# Revit family: Тумба медицинская общего назначения с выдвижным ящиком
name_source: partatom
category: Оборудование
revit_build: Autodesk Revit 2017 (Build: 20170419_0315(x64)
units: mm (PartAtom-declared; Revit-internal decimal feet)

## family parameters
Всегда вертикально = Да
На основе рабочей плоскости = Нет
Общий = Нет
При загрузке вырезать с полостями = Нет
Размер круглого соединителя = Использовать диаметр
Тип детали = Нормальный
Точка расчета площади = Нет

## types (1)
- 400x600x900
    d_опоры = 51 мм
    Высота = 900 мм
    Глубина = 600 мм
    Группа модели = ТХ
    Единицы = шт.
    Завод = Меделия
    Изготовитель = Severin
    Материал доп. = Стол, белый
    Материал опоры = металл с эпоксидным напылением
    Материал основной = Белая краска_01
    Материал столешницы = ДСП с пластиковым покрытием
    Наименование = Тумба медицинская общего назначения стационарная с выдвижным ящиком
    Обозначение = М-ТК-40
    Толщина столешницы = 28 мм
    Ширина = 400 мм

## geometry (parser evidence)
native form markers: Blend x2
no freeform markers — native parametric forms only
